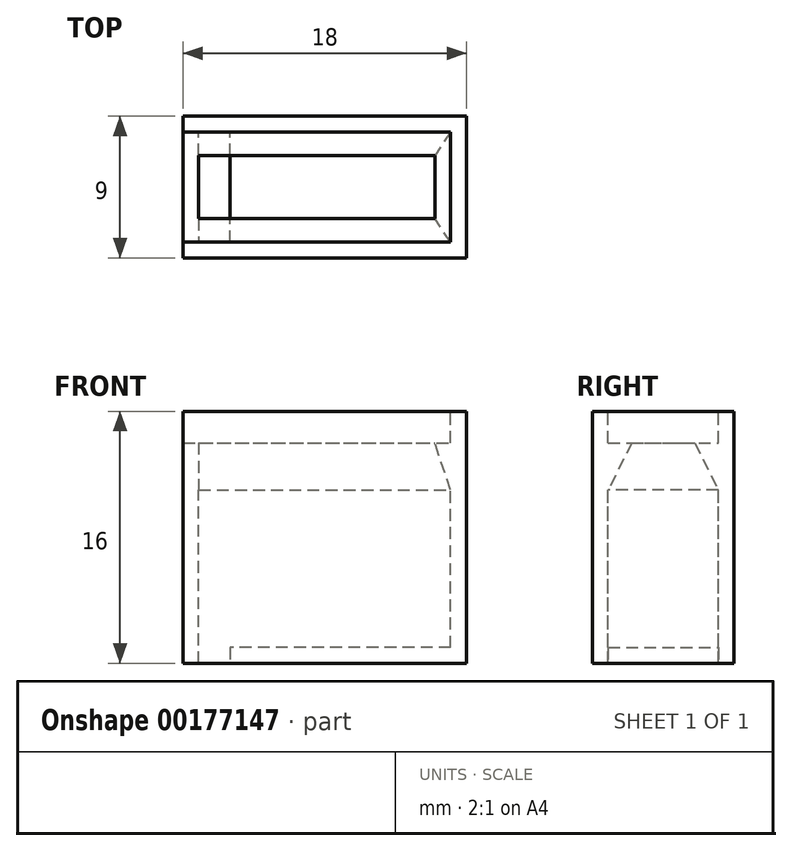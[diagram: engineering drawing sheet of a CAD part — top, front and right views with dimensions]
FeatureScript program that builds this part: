
annotation { "Feature Type Name" : "Feature", "Feature Type Description" : "" }
export const myFeature = defineFeature(function(context is Context, id is Id, definition is map)
    precondition{}
    {
        {
            var Q0;
            Q0=qCreatedBy(makeId("Top.planeOp"),FACE);
            var sketch = newSketch(context, id + "F0", { "sketchPlane" : qUnion([Q0])});
            skLineSegment(sketch, "E0.bottom", {"start": v(9, -4.5) * mm, "end": v(-9, -4.5) * mm});
            skLineSegment(sketch, "E0.top", {"start": v(9, 4.5) * mm, "end": v(-9, 4.5) * mm});
            skLineSegment(sketch, "E0.left", {"start": v(9, -4.5) * mm, "end": v(9, 4.5) * mm});
            skLineSegment(sketch, "E0.right", {"start": v(-9, -4.5) * mm, "end": v(-9, 4.5) * mm});
            skPoint(sketch, "E0.middle", {"position": v(0, 0) * mm});
            skSolve(sketch);
        }
        {
            var Q0;
            Q0=qSketchRegion(id+"F0",true);
            extrude(context, id + "F1", {"entities" : qUnion([Q0]), "depth" : 14 * mm});
        }
        {
            var Q0;
            Q0=makeQuery(id+"F1.opExtrude","CAP_FACE",FACE,{"disambiguationData":[OSD([sQuery(id+"F0.wireOp",EDGE,"E0.bottom"),sQuery(id+"F0.wireOp",EDGE,"E0.top"),sQuery(id+"F0.wireOp",EDGE,"E0.left"),sQuery(id+"F0.wireOp",EDGE,"E0.right")])],"isStart":false});
            var sketch = newSketch(context, id + "F2", { "sketchPlane" : qUnion([Q0])});
            skLineSegment(sketch, "E1.bottom", {"start": v(8, -3.5) * mm, "end": v(-8, -3.5) * mm});
            skLineSegment(sketch, "E1.top", {"start": v(8, 3.5) * mm, "end": v(-8, 3.5) * mm});
            skLineSegment(sketch, "E1.left", {"start": v(8, -3.5) * mm, "end": v(8, 3.5) * mm});
            skLineSegment(sketch, "E1.right", {"start": v(-8, -3.5) * mm, "end": v(-8, 3.5) * mm});
            skPoint(sketch, "E1.middle", {"position": v(0, 0) * mm});
            skSolve(sketch);
        }
        {
            var Q0;
            Q0=qSketchRegion(id+"F2",true);
            extrude(context, id + "F3", {"entities" : qUnion([Q0]), "operationType" : NewBodyOperationType.REMOVE, "oppositeDirection" : true, "depth" : 13 * mm});
        }
        {
            var Q0;
            Q0=makeQuery(id+"F1.opExtrude","CAP_FACE",FACE,{"disambiguationData":[OSD([sQuery(id+"F0.wireOp",EDGE,"E0.bottom"),sQuery(id+"F0.wireOp",EDGE,"E0.top"),sQuery(id+"F0.wireOp",EDGE,"E0.left"),sQuery(id+"F0.wireOp",EDGE,"E0.right")])],"isStart":true});
            var sketch = newSketch(context, id + "F4", { "sketchPlane" : qUnion([Q0])});
            skLineSegment(sketch, "E2.bottom", {"start": v(4.1, -2) * mm, "end": v(0.1, -2) * mm, "construction": true});
            skLineSegment(sketch, "E2.top", {"start": v(4.1, 2) * mm, "end": v(0.1, 2) * mm, "construction": true});
            skLineSegment(sketch, "E2.left", {"start": v(4.1, -2) * mm, "end": v(4.1, 2) * mm, "construction": true});
            skLineSegment(sketch, "E2.right", {"start": v(0.1, -2) * mm, "end": v(0.1, 2) * mm, "construction": true});
            skPoint(sketch, "E2.middle", {"position": v(2.1, 0) * mm});
            skLineSegment(sketch, "E3.bottom", {"start": v(-6, -3.5) * mm, "end": v(-8, -3.5) * mm});
            skLineSegment(sketch, "E3.top", {"start": v(-6, 3.5) * mm, "end": v(-8, 3.5) * mm});
            skLineSegment(sketch, "E3.left", {"start": v(-6, -3.5) * mm, "end": v(-6, 3.5) * mm});
            skLineSegment(sketch, "E3.right", {"start": v(-8, -3.5) * mm, "end": v(-8, 3.5) * mm});
            skPoint(sketch, "E3.middle", {"position": v(-7, 0) * mm});
            skSolve(sketch);
        }
        {
            var Q0;
            Q0 = qSketchRegion(id + "F4", true);
            extrude(context, id + "F5", {"entities" : qUnion([Q0]), "operationType" : NewBodyOperationType.REMOVE, "oppositeDirection" : true, "depth" : 6 * mm});
        }
        {
            var Q0;
            Q0=makeQuery(id+"F4.imprint","IMPRINT",FACE,{"disambiguationData":[TD([[makeQuery(id+"F4.imprint","IMPRINT",EDGE,{"derivedFrom":sQuery(id+"F4.wireOp",EDGE,"E3.bottom")}),-1.0]])]});
            extrude(context, id + "F6", {"entities" : qUnion([Q0]), "operationType" : NewBodyOperationType.REMOVE, "oppositeDirection" : true, "depth" : 9 * mm});
        }
        {
            var Q0;
            Q0=makeQuery(id+"F1.opExtrude","CAP_FACE",FACE,{"disambiguationData":[OSD([sQuery(id+"F0.wireOp",EDGE,"E0.bottom"),sQuery(id+"F0.wireOp",EDGE,"E0.top"),sQuery(id+"F0.wireOp",EDGE,"E0.left"),sQuery(id+"F0.wireOp",EDGE,"E0.right")])],"isStart":false});
            var sketch = newSketch(context, id + "F7", { "sketchPlane" : qUnion([Q0])});
            skLineSegment(sketch, "E4", {"start": v(-9, 4.5) * mm, "end": v(9, 4.5) * mm});
            skLineSegment(sketch, "E5", {"start": v(9, 4.5) * mm, "end": v(9, -4.5) * mm});
            skLineSegment(sketch, "E6", {"start": v(9, -4.5) * mm, "end": v(-9, -4.5) * mm});
            skLineSegment(sketch, "E7", {"start": v(-9, -4.5) * mm, "end": v(-9, -3.5) * mm});
            skLineSegment(sketch, "E8", {"start": v(-9, -3.5) * mm, "end": v(8, -3.5) * mm});
            skLineSegment(sketch, "E9", {"start": v(8, -3.5) * mm, "end": v(8, 3.5) * mm});
            skLineSegment(sketch, "E10", {"start": v(8, 3.5) * mm, "end": v(-9, 3.5) * mm});
            skLineSegment(sketch, "E11", {"start": v(-9, 3.5) * mm, "end": v(-9, 4.5) * mm});
            skSolve(sketch);
        }
        {
            var Q0;
            Q0=qSketchRegion(id+"F7",true);
            extrude(context, id + "F8", {"entities" : qUnion([Q0]), "operationType" : NewBodyOperationType.ADD, "depth" : 2 * mm});
        }
        {
            var Q0;
            Q0=makeQuery(id+"F8.boolean.opBoolean","MERGE",FACE,{"derivedFrom":[makeQuery(id+"F6.boolean.opBoolean","MERGE",FACE,{"derivedFrom":[makeQuery(id+"F3.boolean.opBoolean","COPY",FACE,{"derivedFrom":makeQuery(id+"F3.opExtrude","SWEPT_FACE",FACE,{"disambiguationData":[OSD([sQuery(id+"F2.wireOp",EDGE,"E1.bottom")])]})}),makeQuery(id+"F6.opExtrude","SWEPT_FACE",FACE,{"disambiguationData":[OSD([sQuery(id+"F4.wireOp",EDGE,"E3.top")])]})]}),makeQuery(id+"F8.opExtrude","SWEPT_FACE",FACE,{"disambiguationData":[OSD([sQuery(id+"F7.wireOp",EDGE,"E8")])]})]});
            var sketch = newSketch(context, id + "F9", { "sketchPlane" : qUnion([Q0])});
            skLineSegment(sketch, "E12", {"start": v(-8, 14) * mm, "end": v(-7, 14) * mm});
            skLineSegment(sketch, "E13", {"start": v(8, 14) * mm, "end": v(6.5, 14) * mm, "construction": true});
            skLineSegment(sketch, "E14", {"start": v(6.5, 14) * mm, "end": v(8, 7) * mm, "construction": true});
            skLineSegment(sketch, "E15", {"start": v(8, 7) * mm, "end": v(8, 14) * mm, "construction": true});
            skLineSegment(sketch, "E16", {"start": v(-7, 14) * mm, "end": v(-8, 11) * mm});
            skLineSegment(sketch, "E17", {"start": v(-8, 11) * mm, "end": v(-8, 14) * mm});
            skSolve(sketch);
        }
        {
            var Q0;
            Q0=qSketchRegion(id+"F9",true);
            extrude(context, id + "F10", {"entities" : qUnion([Q0]), "depth" : 7 * mm});
        }
        {
            var Q0;
            Q0=makeQuery(id+"F8.boolean.opBoolean","MERGE",FACE,{"derivedFrom":[makeQuery(id+"F3.boolean.opBoolean","COPY",FACE,{"derivedFrom":makeQuery(id+"F3.opExtrude","SWEPT_FACE",FACE,{"disambiguationData":[OSD([sQuery(id+"F2.wireOp",EDGE,"E1.left")])]})}),makeQuery(id+"F8.opExtrude","SWEPT_FACE",FACE,{"disambiguationData":[OSD([sQuery(id+"F7.wireOp",EDGE,"E9")])]})]});
            var sketch = newSketch(context, id + "F11", { "sketchPlane" : qUnion([Q0])});
            skLineSegment(sketch, "E18", {"start": v(3.5, 14) * mm, "end": v(2, 14) * mm});
            skLineSegment(sketch, "E19", {"start": v(-2, 14) * mm, "end": v(-3.5, 14) * mm});
            skLineSegment(sketch, "E20", {"start": v(2, 14) * mm, "end": v(3.5, 11) * mm});
            skLineSegment(sketch, "E21", {"start": v(3.5, 11) * mm, "end": v(3.5, 14) * mm});
            skLineSegment(sketch, "E22", {"start": v(-2, 14) * mm, "end": v(-3.5, 11) * mm});
            skLineSegment(sketch, "E23", {"start": v(-3.5, 11) * mm, "end": v(-3.5, 14) * mm});
            skSolve(sketch);
        }
        {
            var Q0;
            Q0=qSketchRegion(id+"F11",true);
            extrude(context, id + "F12", {"entities" : qUnion([Q0]), "operationType" : NewBodyOperationType.ADD, "depth" : 16 * mm});
        }
    });
